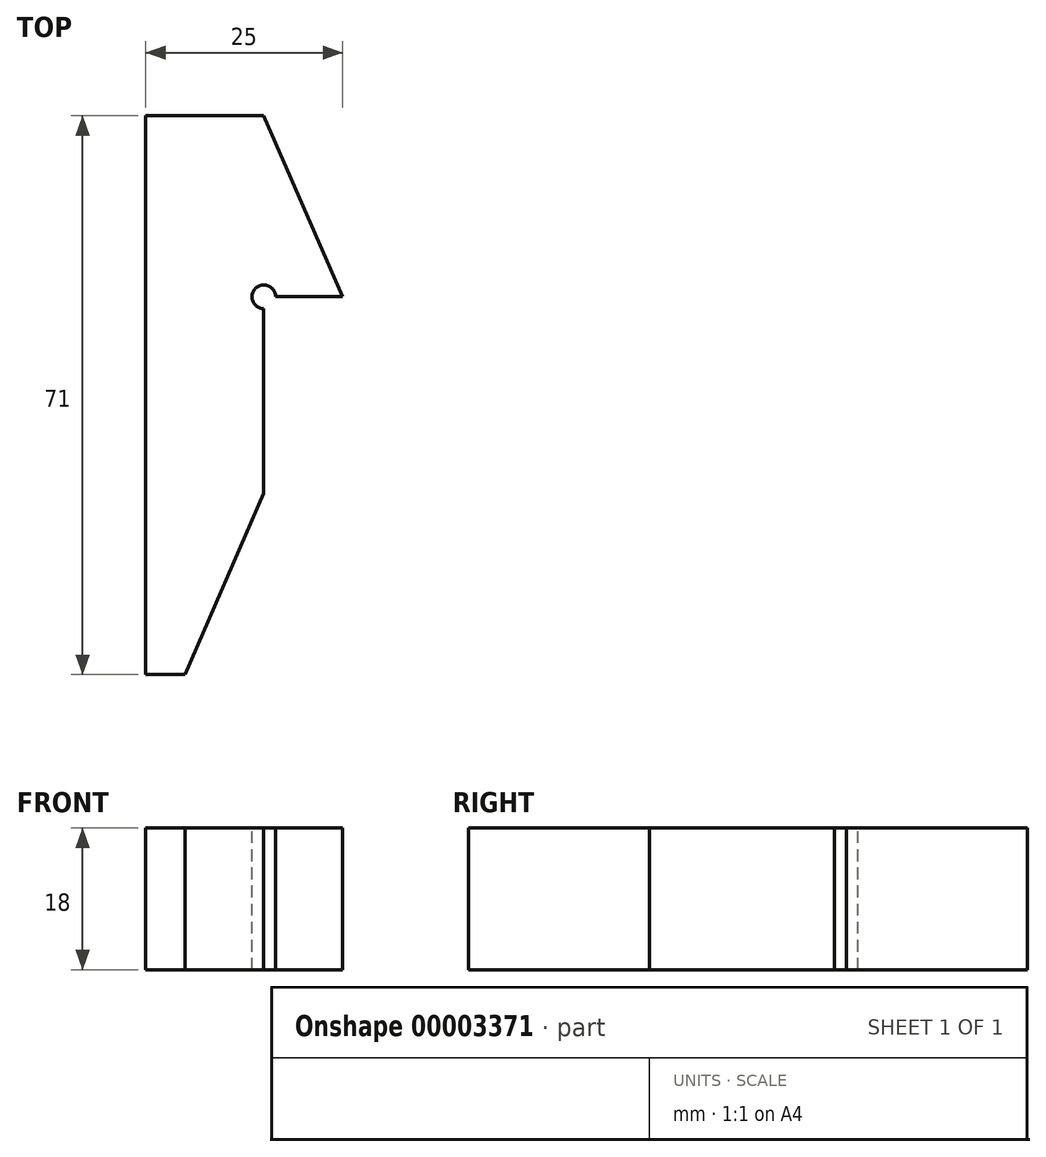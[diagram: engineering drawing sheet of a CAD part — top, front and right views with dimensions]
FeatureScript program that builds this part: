
annotation { "Feature Type Name" : "Feature", "Feature Type Description" : "" }
export const myFeature = defineFeature(function(context is Context, id is Id, definition is map)
    precondition{}
    {
        {
            var Q0;
            Q0=qCreatedBy(makeId("Top.planeOp"),FACE);
            var sketch = newSketch(context, id + "F0", { "sketchPlane" : qUnion([Q0])});
            skLineSegment(sketch, "E0", {"start": v(-241.9, -48) * mm, "end": v(-241.9, 23) * mm});
            skLineSegment(sketch, "E1", {"start": v(-241.9, 23) * mm, "end": v(-226.9, 23) * mm});
            skLineSegment(sketch, "E2", {"start": v(-226.9, 23) * mm, "end": v(-216.9, 0) * mm});
            skLineSegment(sketch, "E3", {"start": v(-216.9, 0) * mm, "end": v(-226.9, 0) * mm});
            skLineSegment(sketch, "E4", {"start": v(-226.9, 0) * mm, "end": v(-226.9, -25) * mm});
            skLineSegment(sketch, "E5", {"start": v(-226.9, -25) * mm, "end": v(-236.9, -48) * mm});
            skLineSegment(sketch, "E6", {"start": v(-236.9, -48) * mm, "end": v(-241.9, -48) * mm});
            skSolve(sketch);
        }
        {
            var Q0;
            Q0=makeQuery(id+"F0.imprint","IMPRINT",FACE,{"disambiguationData":[TD([[makeQuery(id+"F0.imprint","IMPRINT",EDGE,{"derivedFrom":sQuery(id+"F0.wireOp",EDGE,"E0")}),-1.0]])]});
            extrude(context, id + "F1", {"entities" : qUnion([Q0]), "depth" : 18 * mm});
        }
        {
            var Q0;
            Q0=makeQuery(id+"F1.opExtrude","CAP_FACE",FACE,{"disambiguationData":[OSD([sQuery(id+"F0.wireOp",EDGE,"E0"),sQuery(id+"F0.wireOp",EDGE,"E1"),sQuery(id+"F0.wireOp",EDGE,"E2"),sQuery(id+"F0.wireOp",EDGE,"E3"),sQuery(id+"F0.wireOp",EDGE,"E4"),sQuery(id+"F0.wireOp",EDGE,"E5"),sQuery(id+"F0.wireOp",EDGE,"E6")])],"isStart":false});
            var sketch = newSketch(context, id + "F2", { "sketchPlane" : qUnion([Q0])});
            skCircle(sketch, "E7", {"center": v(-226.9, 0) * mm, "radius": 1.5 * mm});
            skSolve(sketch);
        }
        {
            var Q0;
            {var subQ1=sQuery(id+"F2.wireOp",EDGE,"E7");var subQ3=makeQuery(id+"F1.opExtrude","CAP_EDGE",EDGE,{"disambiguationData":[OSD([sQuery(id+"F0.wireOp",EDGE,"E3")])],"isStart":false});var subQ6=makeQuery(id+"F2.imprint","INTERSECT",VERTEX,{"derivedFrom":[subQ3,subQ1]});Q0=qUnion([makeQuery(id+"F2.imprint","IMPRINT",FACE,{"disambiguationData":[TD([[makeQuery(id+"F2.imprint","IMPRINT",EDGE,{"disambiguationData":[TD([[subQ6,1.0]])],"derivedFrom":subQ1}),1.0]])]}),makeQuery(id+"F2.imprint","IMPRINT",FACE,{"disambiguationData":[TD([[makeQuery(id+"F2.imprint","IMPRINT",EDGE,{"disambiguationData":[TD([[subQ6,-1.0]])],"derivedFrom":subQ1}),1.0]])]})]);}
            extrude(context, id + "F3", {"entities" : qUnion([Q0]), "operationType" : NewBodyOperationType.REMOVE, "oppositeDirection" : true, "depth" : 25 * mm});
        }
    });
